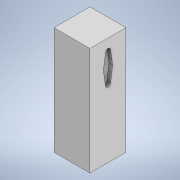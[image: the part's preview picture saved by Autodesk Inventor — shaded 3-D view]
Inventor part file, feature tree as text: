
AUTODESK INVENTOR PART (.ipt)
format: ipt  version: 2021 (Build 250183000, 183)  size: 105,984 bytes
history: native  units: mm
features: extrude x2, sketch x2
ambient origin geometry x8: Origin, YZ Plane, XZ Plane, XY Plane, X Axis, Y Axis, Z Axis, Center Point
bodies: Solid1 (feature_tree)
feature tree (4):
  extrude  "Extrusion1"  Depth=50.0mm
  extrude  "Extrusion2"  Depth=5.0mm
  sketch  "Sketch1"  dims[d0=50.0mm d1=50.0mm]
  sketch  "Sketch2"  dims[d2=150.0mm d3=0.0mm d4=13.0mm d5=7.0mm d6=20.0mm d7=5.0mm d8=0.0mm]
